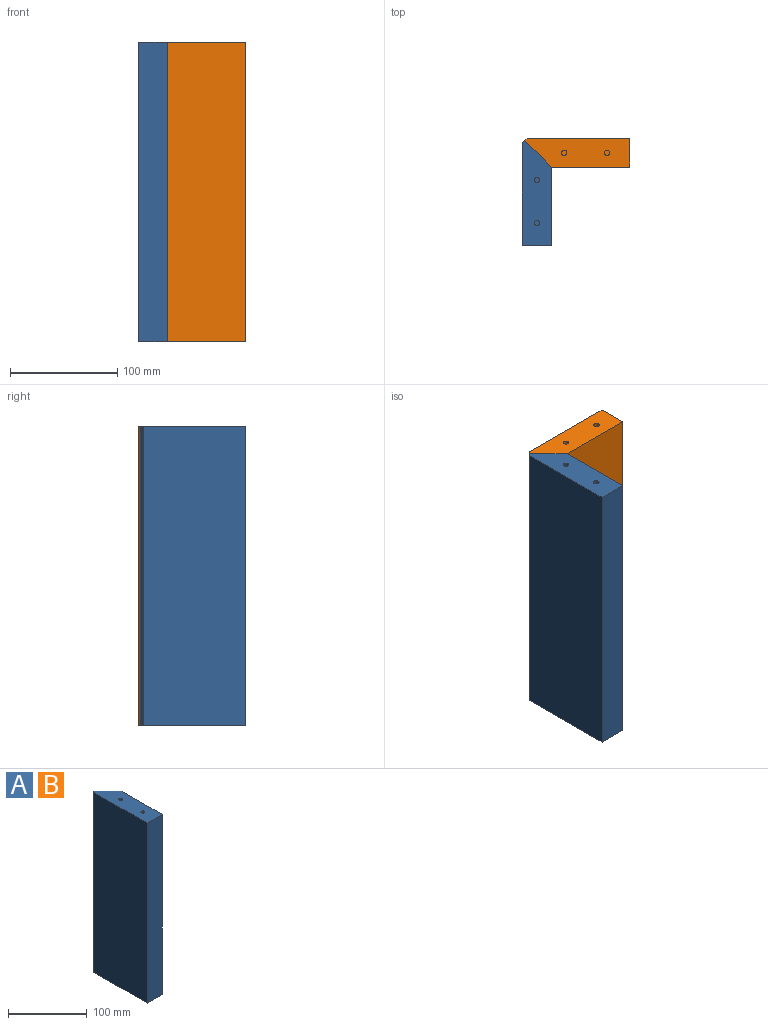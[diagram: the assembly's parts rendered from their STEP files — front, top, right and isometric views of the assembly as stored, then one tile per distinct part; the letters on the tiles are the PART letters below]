
ASSEMBLY  parts=2 mates=1
PART A: 15 faces, bbox 27x97.9x280 mm
  f0: plane 280x95.76mm, normal (-1,0,0), area 26812.1mm2, adj f1,f4,f5,f6
  f1: plane 280x27mm, normal (0,-1,0), area 7560mm2, adj f0,f2,f5,f6
  f2: plane 280x73mm, normal (1,0,0), area 20440mm2, adj f1,f3,f5,f6
  f3: plane 280x24.88mm, normal (0.71,0.71,0), area 9851.5mm2, adj f2,f4,f5,f6
  f4: plane 280x2.12mm, normal (-0.71,0.71,0), area 840mm2, adj f0,f3,f5,f6
  f5: plane 97.88x27mm, normal (0,0,1), area 2291.7mm2, adj f0,f1,f2,f3,f4,f7,f9
  f6: plane 97.88x27mm, normal (0,0,-1), area 2291.7mm2, adj f0,f1,f2,f3,f4,f11,f13
  f7: cylinder r=2.5mm len=25mm, axis (0,0,1), area 392.7mm2, adj f5,f8
  f8: plane 5x5mm, normal (0,0,1), area 19.6mm2, adj f7
  f9: cylinder r=2.5mm len=25mm, axis (0,0,1), area 392.7mm2, adj f5,f10
  f10: plane 5x5mm, normal (0,0,1), area 19.6mm2, adj f9
  f11: cylinder r=2.5mm len=25mm, axis (0,0,-1), area 392.7mm2, adj f6,f12
  f12: plane 5x5mm, normal (0,0,-1), area 19.6mm2, adj f11
  f13: cylinder r=2.5mm len=25mm, axis (0,0,-1), area 392.7mm2, adj f6,f14
  f14: plane 5x5mm, normal (0,0,-1), area 19.6mm2, adj f13
PART B: same geometry as A
PLACE A t=(0,157.03,140)mm
PLACE B rot(axis=(0.71,-0.71,0),180deg) t=(-57.03,100,140)mm
MATE fastened B.f3 <-> A.f3  axis (-0.71,-0.71,0) through (14.56,85.44,140)mm
